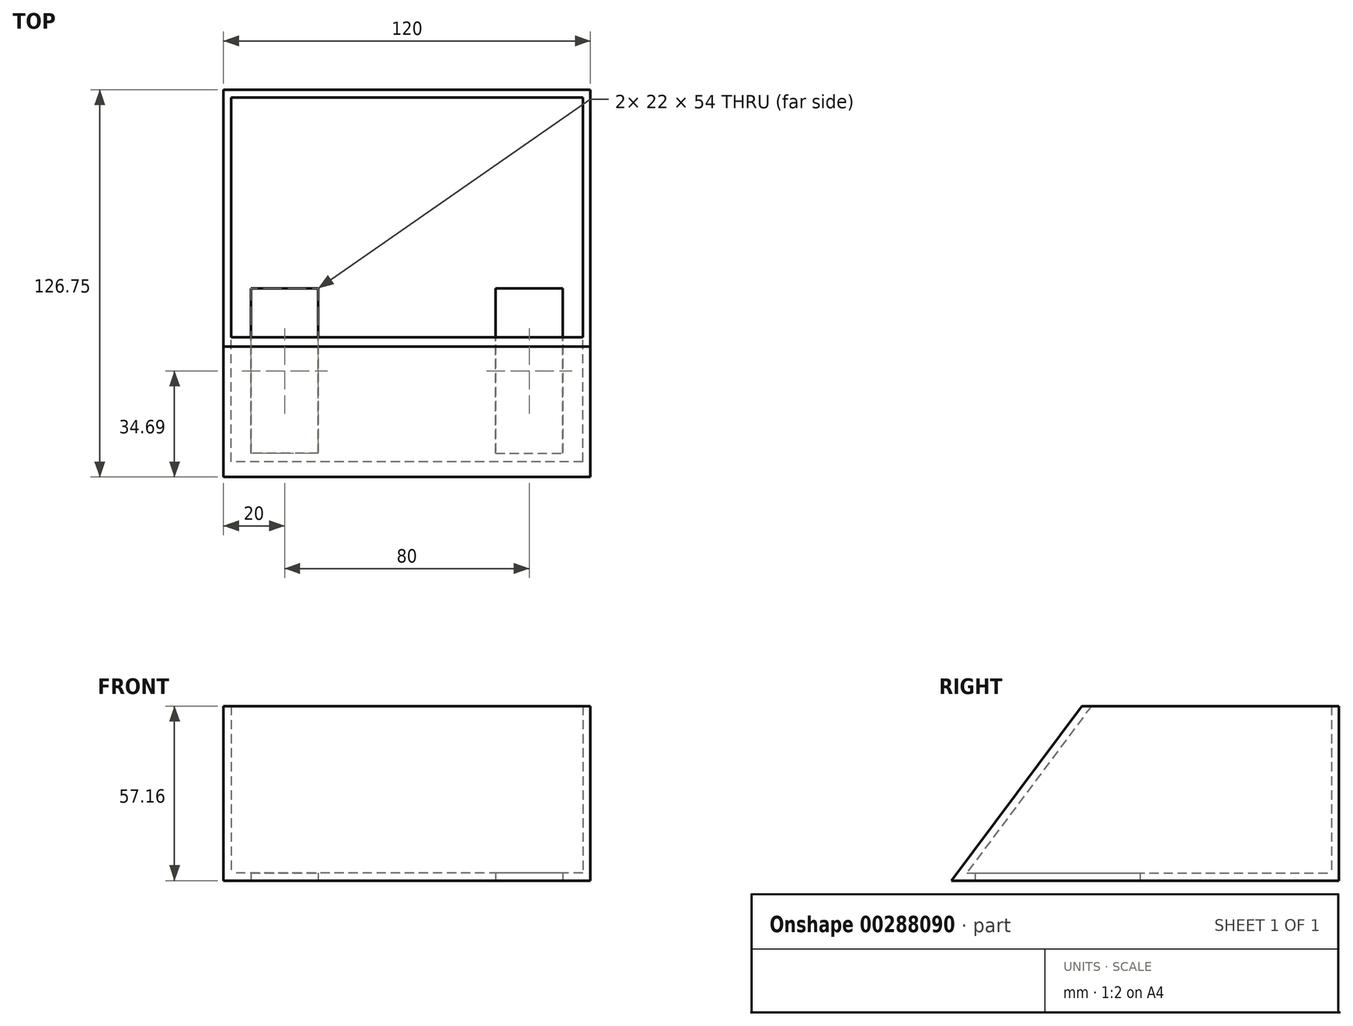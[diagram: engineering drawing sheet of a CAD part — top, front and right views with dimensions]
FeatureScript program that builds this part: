
annotation { "Feature Type Name" : "Feature", "Feature Type Description" : "" }
export const myFeature = defineFeature(function(context is Context, id is Id, definition is map)
    precondition{}
    {
        {
            var Q0;
            Q0=qCreatedBy(makeId("Right.planeOp"),FACE);
            var sketch = newSketch(context, id + "F0", { "sketchPlane" : qUnion([Q0])});
            skLineSegment(sketch, "E0.bottom", {"start": v(42.06, 28.58) * mm, "end": v(-42.06, 28.58) * mm});
            skLineSegment(sketch, "E0.top", {"start": v(42.06, -28.58) * mm, "end": v(-42.06, -28.58) * mm});
            skLineSegment(sketch, "E0.left", {"start": v(42.06, 28.58) * mm, "end": v(42.06, -28.58) * mm});
            skLineSegment(sketch, "E0.right", {"start": v(-42.06, 28.58) * mm, "end": v(-42.06, -28.58) * mm});
            skPoint(sketch, "E0.middle", {"position": v(0, 0) * mm});
            skLineSegment(sketch, "E1", {"start": v(-42.06, 28.58) * mm, "end": v(-84.7, -28.58) * mm});
            skLineSegment(sketch, "E2", {"start": v(-84.7, -28.58) * mm, "end": v(-42.06, -28.58) * mm});
            skSolve(sketch);
        }
        {
            var Q0;
            Q0=makeQuery(id+"F0.imprint","IMPRINT",FACE,{"disambiguationData":[TD([[makeQuery(id+"F0.imprint","IMPRINT",EDGE,{"derivedFrom":sQuery(id+"F0.wireOp",EDGE,"E0.right")}),-1.0]])]});
            extrude(context, id + "F1", {"entities" : qUnion([Q0]), "endBound" : BoundingType.SYMMETRIC, "depth" : 120 * mm});
        }
        {
            var Q0;
            Q0 = qSketchRegion(id + "F0", true);
            extrude(context, id + "F2", {"entities" : qUnion([Q0]), "operationType" : NewBodyOperationType.ADD, "endBound" : BoundingType.SYMMETRIC, "depth" : 120 * mm});
        }
        {
            var Q0;
            Q0=makeQuery(id+"F2.opExtrude","SWEPT_FACE",FACE,{"disambiguationData":[OSD([sQuery(id+"F0.wireOp",EDGE,"E0.bottom")])]});
            shell(context, id + "F3", {"entities" : qUnion([Q0]), "thickness" : 2.5 * mm});
        }
        {
            var Q0;
            {var subQ0=sQuery(id+"F0.wireOp",EDGE,"E2");Q0=makeQuery(id+"F2.boolean.opBoolean","MERGE",FACE,{"derivedFrom":[makeQuery(id+"F1.opExtrude","SWEPT_FACE",FACE,{"disambiguationData":[OSD([subQ0])]}),makeQuery(id+"F2.opExtrude","SWEPT_FACE",FACE,{"disambiguationData":[OSD([sQuery(id+"F0.wireOp",EDGE,"E0.top"),subQ0])]})]});}
            var sketch = newSketch(context, id + "F4", { "sketchPlane" : qUnion([Q0])});
            skLineSegment(sketch, "E3", {"start": v(0, -49.05) * mm, "end": v(0, 91.81) * mm, "construction": true});
            skPoint(sketch, "E3.startSnap0", {"position": v(0, 84.7) * mm});
            skPoint(sketch, "E3.endSnap0", {"position": v(0, 84.7) * mm});
            skLineSegment(sketch, "E4.bottom", {"start": v(-29, 23) * mm, "end": v(-51, 23) * mm});
            skLineSegment(sketch, "E4.top", {"start": v(-29, 77) * mm, "end": v(-51, 77) * mm});
            skLineSegment(sketch, "E4.left", {"start": v(-29, 23) * mm, "end": v(-29, 77) * mm});
            skLineSegment(sketch, "E4.right", {"start": v(-51, 23) * mm, "end": v(-51, 77) * mm});
            skPoint(sketch, "E4.middle", {"position": v(-40, 50) * mm});
            skLineSegment(sketch, "E5.MirrorCS", {"start": v(51, 23) * mm, "end": v(51, 77) * mm});
            skLineSegment(sketch, "E6.MirrorCS", {"start": v(29, 77) * mm, "end": v(51, 77) * mm});
            skLineSegment(sketch, "E7.MirrorCS", {"start": v(29, 23) * mm, "end": v(29, 77) * mm});
            skLineSegment(sketch, "E8.MirrorCS", {"start": v(29, 23) * mm, "end": v(51, 23) * mm});
            skSolve(sketch);
        }
        {
            var Q0;
            Q0 = qSketchRegion(id + "F4", true);
            extrude(context, id + "F5", {"entities" : qUnion([Q0]), "operationType" : NewBodyOperationType.REMOVE, "oppositeDirection" : true, "depth" : 5 * mm});
        }
    });
